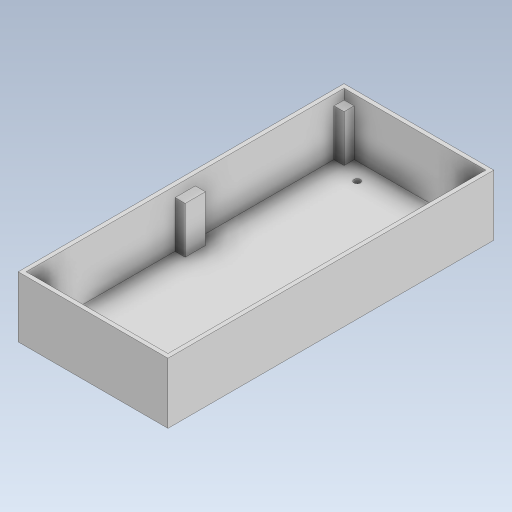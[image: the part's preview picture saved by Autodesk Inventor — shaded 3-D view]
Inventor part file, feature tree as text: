
AUTODESK INVENTOR PART (.ipt)
format: ipt  version: 2023.5 (Build 275446000, 446)  size: 371,712 bytes
history: native  units: mm
features: extrude x3, sketch x1
ambient origin geometry x8: Origin, YZ Plane, XZ Plane, XY Plane, X Axis, Y Axis, Z Axis, Center Point
bodies: Solid1 (feature_tree)
feature tree (4):
  sketch  "Sketch1"  dims[d0=70.0mm d1=157.0mm d2=74.0mm d3=161.0mm d4=3.2mm d5=17.0mm d6=70.0mm d7=5.5mm d8=3.2mm d9=5.5mm d10=34.0mm d11=5.0mm d12=5.0mm d13=5.0mm d14=5.0mm d15=5.0mm d16=5.0mm d17=5.0mm d18=2.0mm d19=0.0mm d20=25.0mm d21=0.0mm d22=30.0mm d23=0.0mm]
  extrude  "Extrusion1"  Depth=157.0mm
  extrude  "Extrusion2"  Depth=74.0mm
  extrude  "Extrusion3"  Depth=161.0mm
